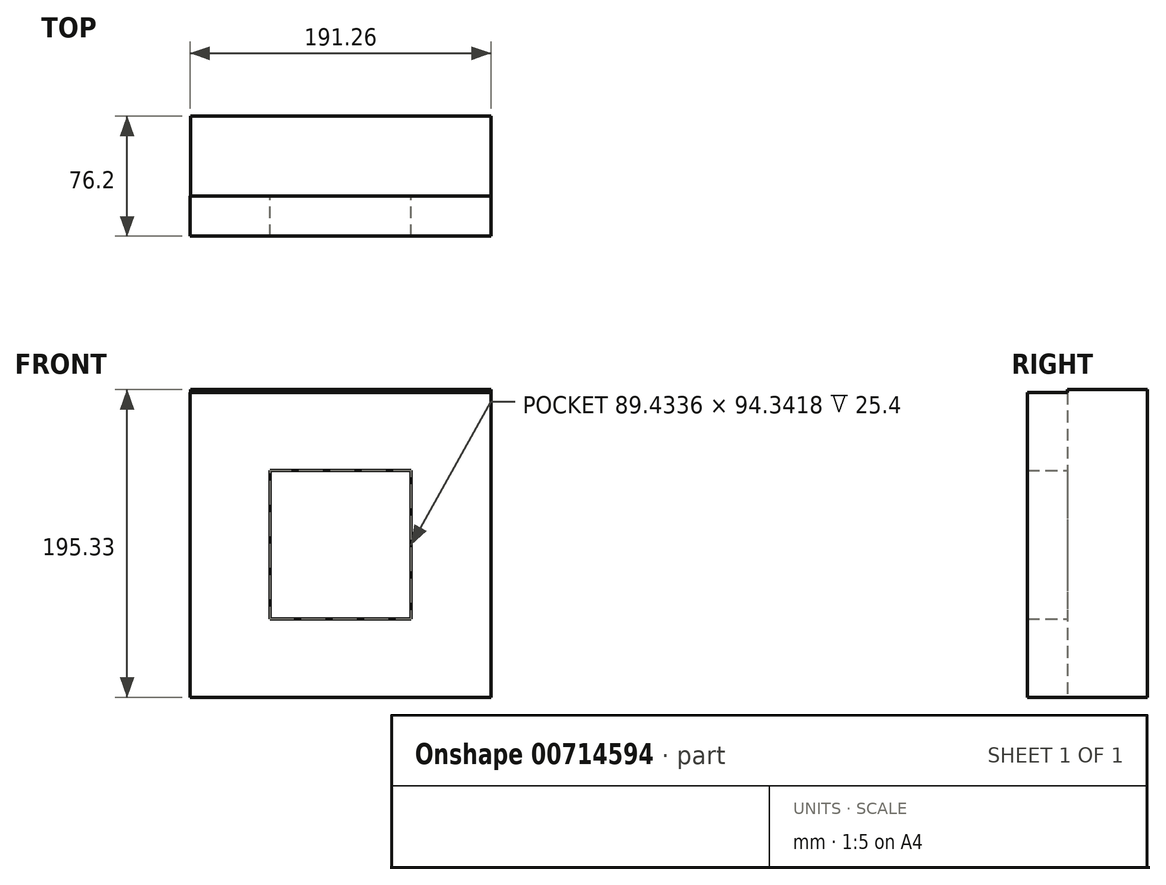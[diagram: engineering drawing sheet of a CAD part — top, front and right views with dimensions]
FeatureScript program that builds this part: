
annotation { "Feature Type Name" : "Feature", "Feature Type Description" : "" }
export const myFeature = defineFeature(function(context is Context, id is Id, definition is map)
    precondition{}
    {
        {
            var Q0;
            Q0=qCreatedBy(makeId("Front.planeOp"),FACE);
            var sketch = newSketch(context, id + "F0", { "sketchPlane" : qUnion([Q0])});
            skLineSegment(sketch, "E0.bottom", {"start": v(95.63, 98.55) * mm, "end": v(-95.35, 98.55) * mm});
            skLineSegment(sketch, "E0.top", {"start": v(95.63, -96.78) * mm, "end": v(-95.35, -96.78) * mm});
            skLineSegment(sketch, "E0.left", {"start": v(95.63, 98.55) * mm, "end": v(95.63, -96.78) * mm});
            skLineSegment(sketch, "E0.right", {"start": v(-95.35, 98.55) * mm, "end": v(-95.35, -96.78) * mm});
            skSolve(sketch);
        }
        {
            var Q0;
            Q0 = qSketchRegion(id + "F0", true);
            extrude(context, id + "F1", {"entities" : qUnion([Q0]), "depth" : 25.4 * mm, "offsetDistance" : 25.4 * mm});
        }
        {
            var Q0;
            Q0=makeQuery(id+"F1.opExtrude","CAP_FACE",FACE,{"disambiguationData":[OSD([sQuery(id+"F0.wireOp",EDGE,"E0.bottom"),sQuery(id+"F0.wireOp",EDGE,"E0.top"),sQuery(id+"F0.wireOp",EDGE,"E0.left"),sQuery(id+"F0.wireOp",EDGE,"E0.right")])],"isStart":true});
            var sketch = newSketch(context, id + "F2", { "sketchPlane" : qUnion([Q0])});
            skLineSegment(sketch, "E1.bottom", {"start": v(46.04, 45.09) * mm, "end": v(-46.04, 45.09) * mm});
            skLineSegment(sketch, "E1.top", {"start": v(46.04, -45.09) * mm, "end": v(-46.04, -45.09) * mm});
            skLineSegment(sketch, "E1.left", {"start": v(46.04, 45.09) * mm, "end": v(46.04, -45.09) * mm});
            skLineSegment(sketch, "E1.right", {"start": v(-46.04, 45.09) * mm, "end": v(-46.04, -45.09) * mm});
            skPoint(sketch, "E1.middle", {"position": v(0, 0) * mm});
            skLineSegment(sketch, "E2.bottom", {"start": v(95.35, 98.55) * mm, "end": v(-95.63, 98.55) * mm});
            skLineSegment(sketch, "E2.top", {"start": v(95.35, -96.78) * mm, "end": v(-95.63, -96.78) * mm});
            skLineSegment(sketch, "E2.left", {"start": v(95.35, 98.55) * mm, "end": v(95.35, -96.78) * mm});
            skLineSegment(sketch, "E2.right", {"start": v(-95.63, 98.55) * mm, "end": v(-95.63, -96.78) * mm});
            skSolve(sketch);
        }
        {
            var Q0;
            Q0 = qSketchRegion(id + "F2", true);
            extrude(context, id + "F3", {"entities" : qUnion([Q0]), "operationType" : NewBodyOperationType.ADD, "depth" : 25.4 * mm, "offsetDistance" : 25.4 * mm});
        }
        {
            var Q0;
            Q0=makeQuery(id+"F1.opExtrude","CAP_FACE",FACE,{"disambiguationData":[OSD([sQuery(id+"F0.wireOp",EDGE,"E0.bottom"),sQuery(id+"F0.wireOp",EDGE,"E0.top"),sQuery(id+"F0.wireOp",EDGE,"E0.left"),sQuery(id+"F0.wireOp",EDGE,"E0.right")])],"isStart":false});
            var sketch = newSketch(context, id + "F4", { "sketchPlane" : qUnion([Q0])});
            skLineSegment(sketch, "E3.bottom", {"start": v(44.72, 47.17) * mm, "end": v(-44.72, 47.17) * mm});
            skLineSegment(sketch, "E3.top", {"start": v(44.72, -47.17) * mm, "end": v(-44.72, -47.17) * mm});
            skLineSegment(sketch, "E3.left", {"start": v(44.72, 47.17) * mm, "end": v(44.72, -47.17) * mm});
            skLineSegment(sketch, "E3.right", {"start": v(-44.72, 47.17) * mm, "end": v(-44.72, -47.17) * mm});
            skPoint(sketch, "E3.middle", {"position": v(0, 0) * mm});
            skLineSegment(sketch, "E4.bottom", {"start": v(95.63, -96.78) * mm, "end": v(-95.63, -96.78) * mm});
            skLineSegment(sketch, "E4.top", {"start": v(95.63, 96.78) * mm, "end": v(-95.63, 96.78) * mm});
            skLineSegment(sketch, "E4.left", {"start": v(95.63, -96.78) * mm, "end": v(95.63, 96.78) * mm});
            skLineSegment(sketch, "E4.right", {"start": v(-95.63, -96.78) * mm, "end": v(-95.63, 96.78) * mm});
            skSolve(sketch);
        }
        {
            var Q0;
            Q0 = qSketchRegion(id + "F4", true);
            extrude(context, id + "F5", {"entities" : qUnion([Q0]), "operationType" : NewBodyOperationType.ADD, "depth" : 25.4 * mm, "offsetDistance" : 25.4 * mm});
        }
        {
            var Q0;
            Q0=makeQuery(id+"F1.opExtrude","CAP_FACE",FACE,{"disambiguationData":[OSD([sQuery(id+"F0.wireOp",EDGE,"E0.bottom"),sQuery(id+"F0.wireOp",EDGE,"E0.top"),sQuery(id+"F0.wireOp",EDGE,"E0.left"),sQuery(id+"F0.wireOp",EDGE,"E0.right")])],"isStart":true});
            var sketch = newSketch(context, id + "F6", { "sketchPlane" : qUnion([Q0])});
            skLineSegment(sketch, "E5.bottom", {"start": v(46.04, -45.09) * mm, "end": v(-46.04, -45.09) * mm});
            skLineSegment(sketch, "E5.top", {"start": v(46.04, 45.09) * mm, "end": v(-46.04, 45.09) * mm});
            skLineSegment(sketch, "E5.left", {"start": v(46.04, -45.09) * mm, "end": v(46.04, 45.09) * mm});
            skLineSegment(sketch, "E5.right", {"start": v(-46.04, -45.09) * mm, "end": v(-46.04, 45.09) * mm});
            skPoint(sketch, "E5.middle", {"position": v(0, 0) * mm});
            skSolve(sketch);
        }
        {
            var Q0;
            Q0 = qSketchRegion(id + "F6", true);
            extrude(context, id + "F7", {"entities" : qUnion([Q0]), "operationType" : NewBodyOperationType.ADD, "depth" : 25.4 * mm, "offsetDistance" : 25.4 * mm});
        }
    });
